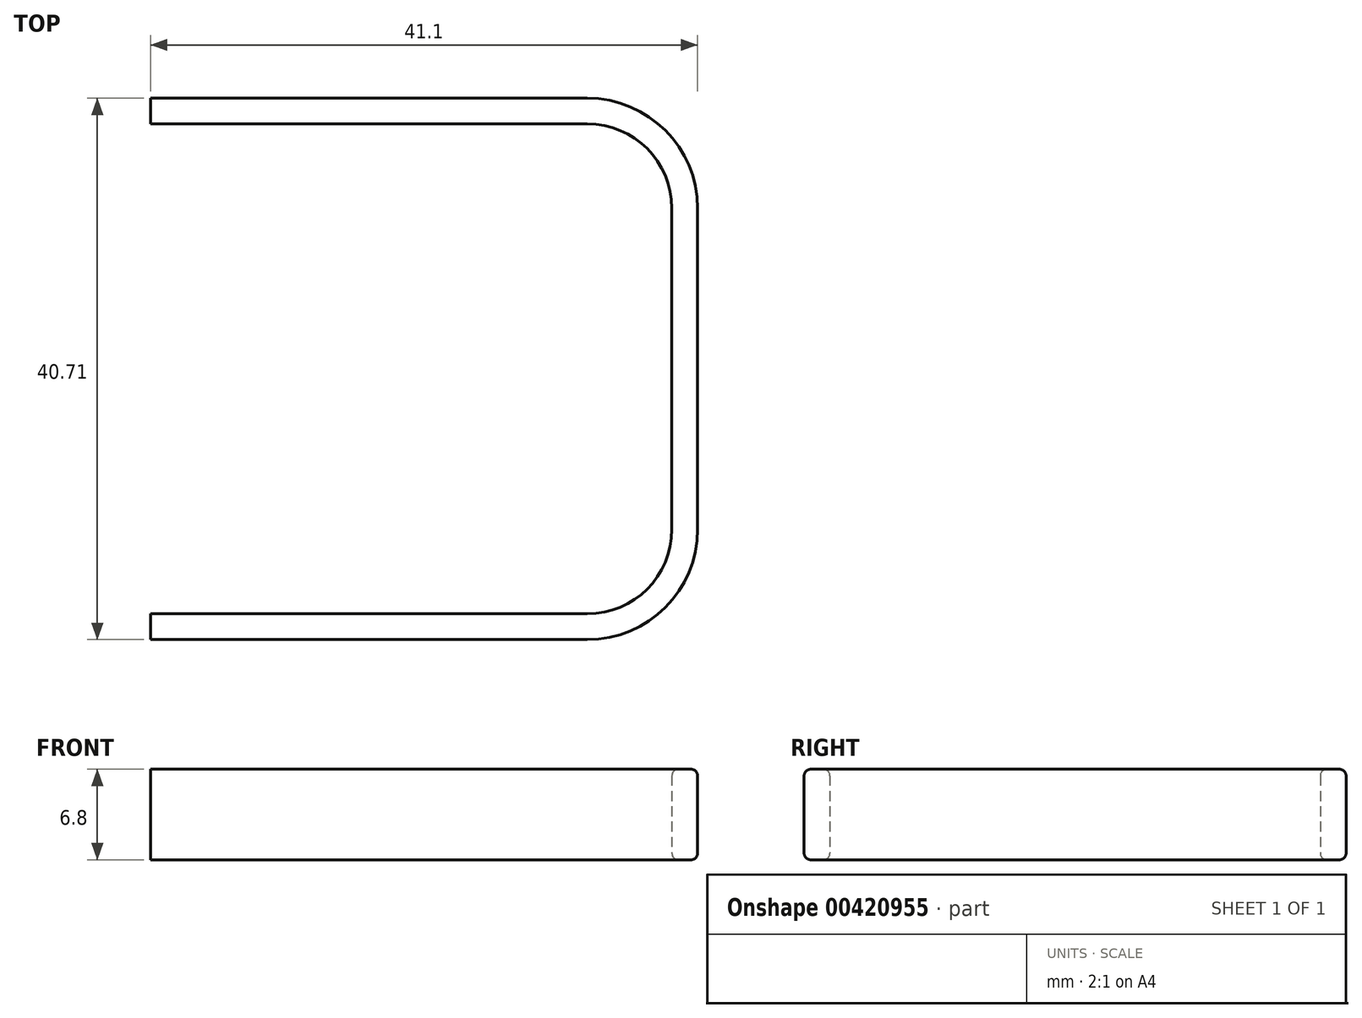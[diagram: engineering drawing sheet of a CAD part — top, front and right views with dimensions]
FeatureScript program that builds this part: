
annotation { "Feature Type Name" : "Feature", "Feature Type Description" : "" }
export const myFeature = defineFeature(function(context is Context, id is Id, definition is map)
    precondition{}
    {
        {
            var Q0;
            Q0=qCreatedBy(makeId("Top.planeOp"),FACE);
            var sketch = newSketch(context, id + "F0", { "sketchPlane" : qUnion([Q0])});
            skLineSegment(sketch, "E0", {"start": v(0, 0) * mm, "end": v(32.82, 0) * mm});
            skLineSegment(sketch, "E1", {"start": v(39.17, -6.35) * mm, "end": v(39.17, -30.5) * mm});
            skLineSegment(sketch, "E2", {"start": v(32.82, -36.85) * mm, "end": v(0, -36.85) * mm});
            skPoint(sketch, "E3.visualSharp", {"position": v(39.17, 0) * mm});
            skArc(sketch, "E3.filletArc", {"start": v(39.17, -6.35) * mm, "mid": v(37.3, -1.86) * mm, "end": v(32.82, 0) * mm});
            skPoint(sketch, "E4.visualSharp", {"position": v(39.17, -36.85) * mm});
            skArc(sketch, "E4.filletArc", {"start": v(32.82, -36.85) * mm, "mid": v(37.3, -34.99) * mm, "end": v(39.17, -30.5) * mm});
            skSolve(sketch);
        }
        {
            var Q0;
            Q0=qCreatedBy(makeId("Right.planeOp"),FACE);
            var sketch = newSketch(context, id + "F1", { "sketchPlane" : qUnion([Q0])});
            skLineSegment(sketch, "E5.bottom", {"start": v(0.49, 0) * mm, "end": v(1.45, 0) * mm});
            skLineSegment(sketch, "E5.top", {"start": v(0.49, -6.8) * mm, "end": v(1.45, -6.8) * mm});
            skLineSegment(sketch, "E5.left", {"start": v(0, -0.49) * mm, "end": v(0, -6.31) * mm});
            skLineSegment(sketch, "E5.right", {"start": v(1.93, -0.49) * mm, "end": v(1.93, -6.31) * mm});
            skPoint(sketch, "E6.visualSharp", {"position": v(0, -6.8) * mm});
            skArc(sketch, "E6.filletArc", {"start": v(0, -6.31) * mm, "mid": v(0.14, -6.66) * mm, "end": v(0.49, -6.8) * mm});
            skPoint(sketch, "E7.visualSharp", {"position": v(1.93, -6.8) * mm});
            skArc(sketch, "E7.filletArc", {"start": v(1.45, -6.8) * mm, "mid": v(1.79, -6.66) * mm, "end": v(1.93, -6.31) * mm});
            skPoint(sketch, "E8.visualSharp", {"position": v(1.93, 0) * mm});
            skArc(sketch, "E8.filletArc", {"start": v(1.93, -0.49) * mm, "mid": v(1.79, -0.14) * mm, "end": v(1.45, 0) * mm});
            skPoint(sketch, "E9.visualSharp", {"position": v(0, 0) * mm});
            skArc(sketch, "E9.filletArc", {"start": v(0.49, 0) * mm, "mid": v(0.14, -0.14) * mm, "end": v(0, -0.49) * mm});
            skSolve(sketch);
        }
        {
            var Q0;
            Q0=makeQuery(id+"F1.imprint","IMPRINT",FACE,{"disambiguationData":[TD([[makeQuery(id+"F1.imprint","IMPRINT",EDGE,{"derivedFrom":sQuery(id+"F1.wireOp",EDGE,"E5.bottom")}),-1.0]])]});
            var Q1;
            Q1=sQuery(id+"F0.wireOp",EDGE,"E0");
            var Q2;
            Q2=sQuery(id+"F0.wireOp",EDGE,"E3.filletArc");
            var Q3;
            Q3=sQuery(id+"F0.wireOp",EDGE,"E1");
            var Q4;
            Q4=sQuery(id+"F0.wireOp",EDGE,"E4.filletArc");
            var Q5;
            Q5=sQuery(id+"F0.wireOp",EDGE,"E2");
            sweep(context, id + "F2", {"profiles" : qUnion([Q0]), "path" : qUnion([Q1, Q2, Q3, Q4, Q5])});
        }
    });
